# Revit family: QF_ADVENTYS_ADV1548-B_GL3000FLR
name_source: partatom
category: Attrezzature speciali
units: mm (PartAtom-declared; Revit-internal decimal feet)

## family parameters
Condiviso = No
Host = Superficie
Punto di calcolo locali = No
Quota connettore circolare = Usa diametro
Taglio con vuoti quando caricato = No
Tipo di parte = Normale

## types (1)
- ADV1548-B
    Controller_Height = 98 mm  [stored 0.321522 ft]
    Controller_Width = 228 mm  [stored 0.748031 ft]
    Cycle = 50 Hz
    Depth = 340 mm  [stored 1.11549 ft]
    Depth Actual = 340 mm  [stored 1.11549 ft]
    Height = 172 mm  [stored 0.564304 ft]
    Height Actual = 172 mm  [stored 0.564304 ft]
    Item Number = ADV1548-B
    Length Actual = 340 mm  [stored 1.11549 ft]
    Modello = GL3000FLR
    Phase = 1
    Produttore = ADVENTYS
    Prospetto di default = 1219.2 mm  [stored 4 ft]
    URL = https://adventys.com
    Volts = 220 V
    Watts = 3000 W
    Weight = 8
    Width = 340 mm  [stored 1.11549 ft]

note: [stored X ft] marks values corroborated as IEEE doubles in the binary element streams (Revit-internal decimal feet)
